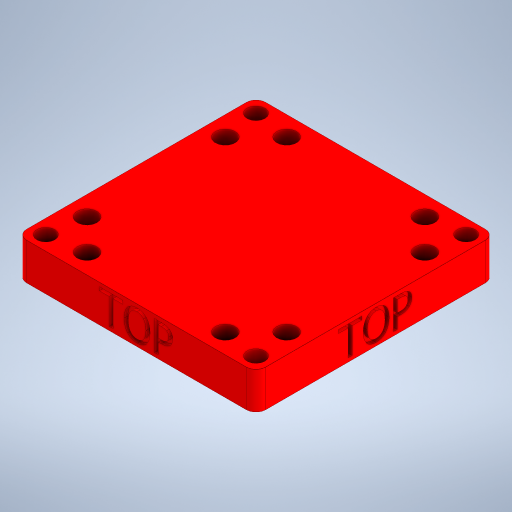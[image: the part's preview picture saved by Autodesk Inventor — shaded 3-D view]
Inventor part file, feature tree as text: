
AUTODESK INVENTOR PART (.ipt)
format: ipt  version: 2023.1 (Build 271208000, 208)  size: 557,568 bytes
history: native  units: mm
features: extrude x6, sketch x3, chamfer x2, projected_geometry x2, fillet x1, pattern_circular x1
ambient origin geometry x8: Origin, YZ Plane, XZ Plane, XY Plane, X Axis, Y Axis, Z Axis, Center Point
bodies: Solid1 (feature_tree)
feature tree (15):
  sketch  "Sketch1"  dims[d0=49.8mm d1=49.8mm]
  extrude  "Extrusion1"  Depth=49.8mm
  extrude  "Extrusion2"  Depth=3.0mm
  chamfer  "Chamfer1"  Distance=3.75mm
  fillet  "Fillet1"  Radius=4.2125mm
  chamfer  "Chamfer2"  Distance=0.675mm
  extrude  "Extrusion3"  Depth=5.5mm
  extrude  "Extrusion4"  Depth=5.5mm
  extrude  "Extrusion5"  Depth=5.5mm
  pattern_circular  "Circular Pattern1"  [2 undecoded]
  extrude  "Extrusion6"  Depth=5.5mm
  sketch  "Sketch2"  dims[d2=7.85mm d3=3.0mm]
  sketch  "Sketch3"  dims[d4=3.0mm d5=3.75mm d6=4.2125mm d7=0.675mm d8=10.5mm d9=10.5mm d10=4.1mm d11=4.14675mm d12=7.85mm d13=7.85mm d14=5.5mm d15=5.5mm d16=40.0mm d18=360.0deg d20=7.7mm d21=0.0mm d22=2.2mm d23=0.0mm d24=5.5mm d25=2.0mm d26=45.0deg d27=2.0mm d28=0.025mm d29=2.0mm d30=45.0deg d31=3.0mm d32=0.0mm d33=3.0mm d34=0.0mm d35=0.75mm d36=0.0mm d37=40.0mm d38=360.0deg d40=2.2mm d41=0.0mm d42=0.5mm d43=0.872665mm d44=0.5mm d45=0.872665mm]
  projected_geometry  "Projected Loop2"
  projected_geometry  "Projected Loop3"
note: 2 required parameter values undecoded (feature->parameter linkage not recoverable at this tier; creation-order binding heuristic only, values carry confidence <= 0.55)
